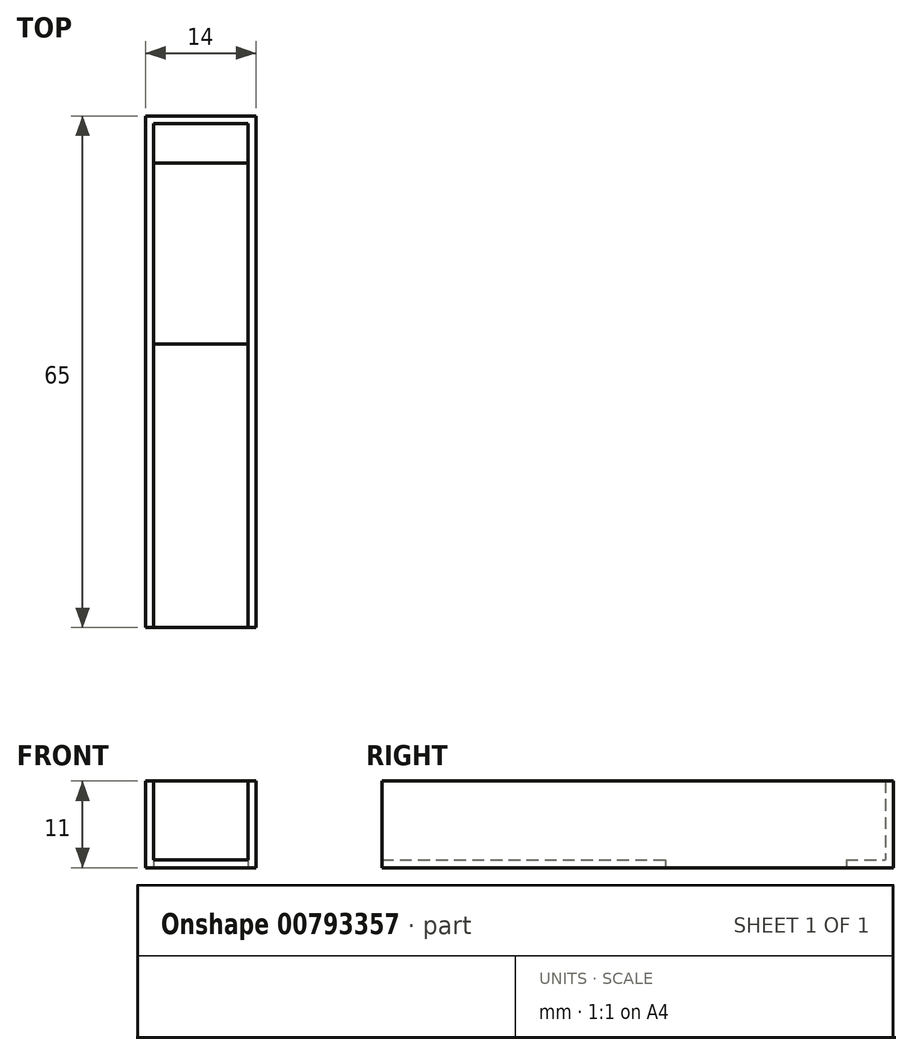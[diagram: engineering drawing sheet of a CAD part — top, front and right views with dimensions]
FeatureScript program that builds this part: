
annotation { "Feature Type Name" : "Feature", "Feature Type Description" : "" }
export const myFeature = defineFeature(function(context is Context, id is Id, definition is map)
    precondition{}
    {
        {
            assignVariable(context, id + "F0", {"name" : "WALL_THICK", "anyValue" : 1});
        }
        {
            var Q0;
            Q0=qCreatedBy(makeId("Top.planeOp"),FACE);
            var sketch = newSketch(context, id + "F1", { "sketchPlane" : qUnion([Q0])});
            skLineSegment(sketch, "E0.bottom", {"start": v(0, 0) * mm, "end": v(14, 0) * mm});
            skLineSegment(sketch, "E0.top", {"start": v(0, -65) * mm, "end": v(14, -65) * mm});
            skLineSegment(sketch, "E0.left", {"start": v(0, 0) * mm, "end": v(0, -65) * mm});
            skLineSegment(sketch, "E0.right", {"start": v(14, 0) * mm, "end": v(14, -65) * mm});
            skLineSegment(sketch, "E1.bottom", {"start": v(1, -6) * mm, "end": v(13, -6) * mm});
            skLineSegment(sketch, "E1.top", {"start": v(1, -29) * mm, "end": v(13, -29) * mm});
            skLineSegment(sketch, "E1.left", {"start": v(1, -6) * mm, "end": v(1, -29) * mm});
            skLineSegment(sketch, "E1.right", {"start": v(13, -6) * mm, "end": v(13, -29) * mm});
            skSolve(sketch);
        }
        {
            var Q0;
            Q0=makeQuery(id+"F1.imprint","IMPRINT",FACE,{"disambiguationData":[TD([[makeQuery(id+"F1.imprint","IMPRINT",EDGE,{"derivedFrom":sQuery(id+"F1.wireOp",EDGE,"E0.bottom")}),-1.0]])]});
            extrude(context, id + "F2", {"entities" : qUnion([Q0]), "depth" : (getVariable(context, 'WALL_THICK')) * mm, "offsetDistance" : 25 * mm});
        }
        {
            var Q0;
            Q0=makeQuery(id+"F2.opExtrude","CAP_FACE",FACE,{"disambiguationData":[OSD([sQuery(id+"F1.wireOp",EDGE,"E0.bottom"),sQuery(id+"F1.wireOp",EDGE,"E0.top"),sQuery(id+"F1.wireOp",EDGE,"E0.left"),sQuery(id+"F1.wireOp",EDGE,"E0.right"),sQuery(id+"F1.wireOp",EDGE,"E1.bottom"),sQuery(id+"F1.wireOp",EDGE,"E1.top"),sQuery(id+"F1.wireOp",EDGE,"E1.left"),sQuery(id+"F1.wireOp",EDGE,"E1.right")])],"isStart":false});
            var sketch = newSketch(context, id + "F3", { "sketchPlane" : qUnion([Q0])});
            skLineSegment(sketch, "E2", {"start": v(0, -65) * mm, "end": v(0, 0) * mm});
            skLineSegment(sketch, "E3", {"start": v(0, 0) * mm, "end": v(14, 0) * mm});
            skLineSegment(sketch, "E4", {"start": v(14, 0) * mm, "end": v(14, -65) * mm});
            skLineSegment(sketch, "E5", {"start": v(14, -65) * mm, "end": v(13, -65) * mm});
            skLineSegment(sketch, "E6", {"start": v(13, -65) * mm, "end": v(13, -1) * mm});
            skLineSegment(sketch, "E7", {"start": v(13, -1) * mm, "end": v(1, -1) * mm});
            skLineSegment(sketch, "E8", {"start": v(1, -1) * mm, "end": v(1, -65) * mm});
            skLineSegment(sketch, "E9", {"start": v(1, -65) * mm, "end": v(0, -65) * mm});
            skSolve(sketch);
        }
        {
            var Q0;
            Q0=makeQuery(id+"F3.imprint","IMPRINT",FACE,{"disambiguationData":[TD([[makeQuery(id+"F3.imprint","IMPRINT",EDGE,{"derivedFrom":sQuery(id+"F3.wireOp",EDGE,"E2")}),1.0]])]});
            extrude(context, id + "F4", {"entities" : qUnion([Q0]), "operationType" : NewBodyOperationType.ADD, "depth" : 10 * mm, "offsetDistance" : 25 * mm});
        }
    });
